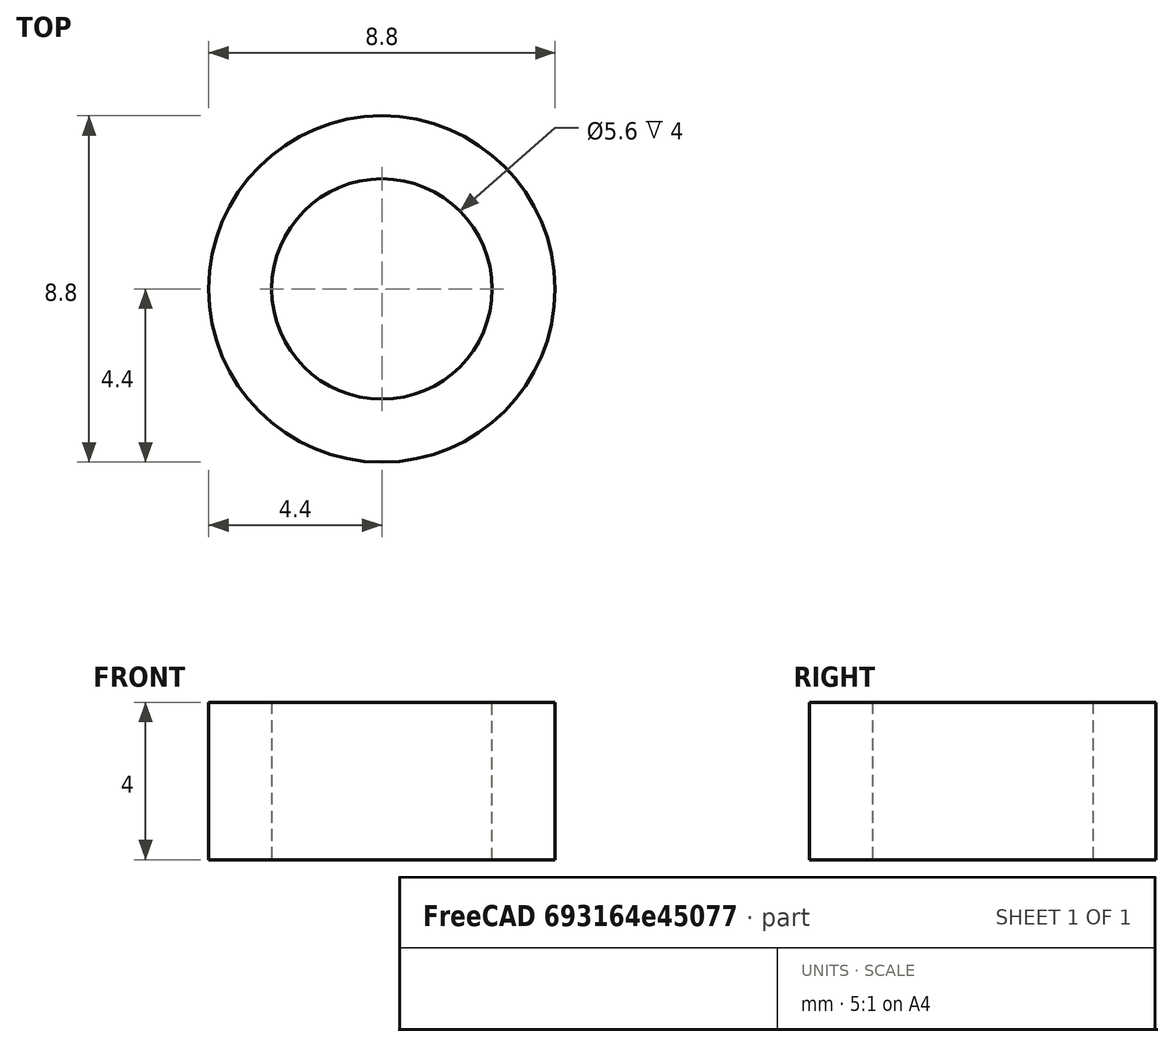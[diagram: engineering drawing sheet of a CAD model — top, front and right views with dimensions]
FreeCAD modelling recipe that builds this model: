
FCSTD DOCUMENT  (FreeCAD 0.18R16146 (Git))
Label: hubSpacer
License: All rights reserved
LicenseURL: http://en.wikipedia.org/wiki/All_rights_reserved
objects: Sketcher::SketchObject×1, PartDesign::Pad×1, PartDesign::Body×1
note: 4 computed .brp shape members not serialized (recipe doc carries the construction recipe); baked Part::Feature solids carry a one-line shape summary decoded from their .brp

FEATURE [Sketcher::SketchObject] Sketch
  MapMode = 5
  Support = -> [XY_Plane]
  sketch-geometry (2):
    g0: Circle CenterX=0 CenterY=0 CenterZ=0 NormalX=0 NormalY=0 NormalZ=1 AngleXU=0 Radius=2.8
    g1: Circle CenterX=0 CenterY=0 CenterZ=0 NormalX=0 NormalY=0 NormalZ=1 AngleXU=0 Radius=4.4
  constraints (4):
    c: Coincident(g0,g-1)
    c: Coincident(g1,g-1)
    c: Radius(g1) = 4.4
    c: Radius(g0) = 2.8
FEATURE [PartDesign::Pad] Pad
  Length = 4
  Length2 = 100
  Profile = -> Sketch
  Type = 0
FEATURE [PartDesign::Body] Body
  Group = -> [Sketch,Pad]
  Origin = -> Origin
  Tip = -> Pad
